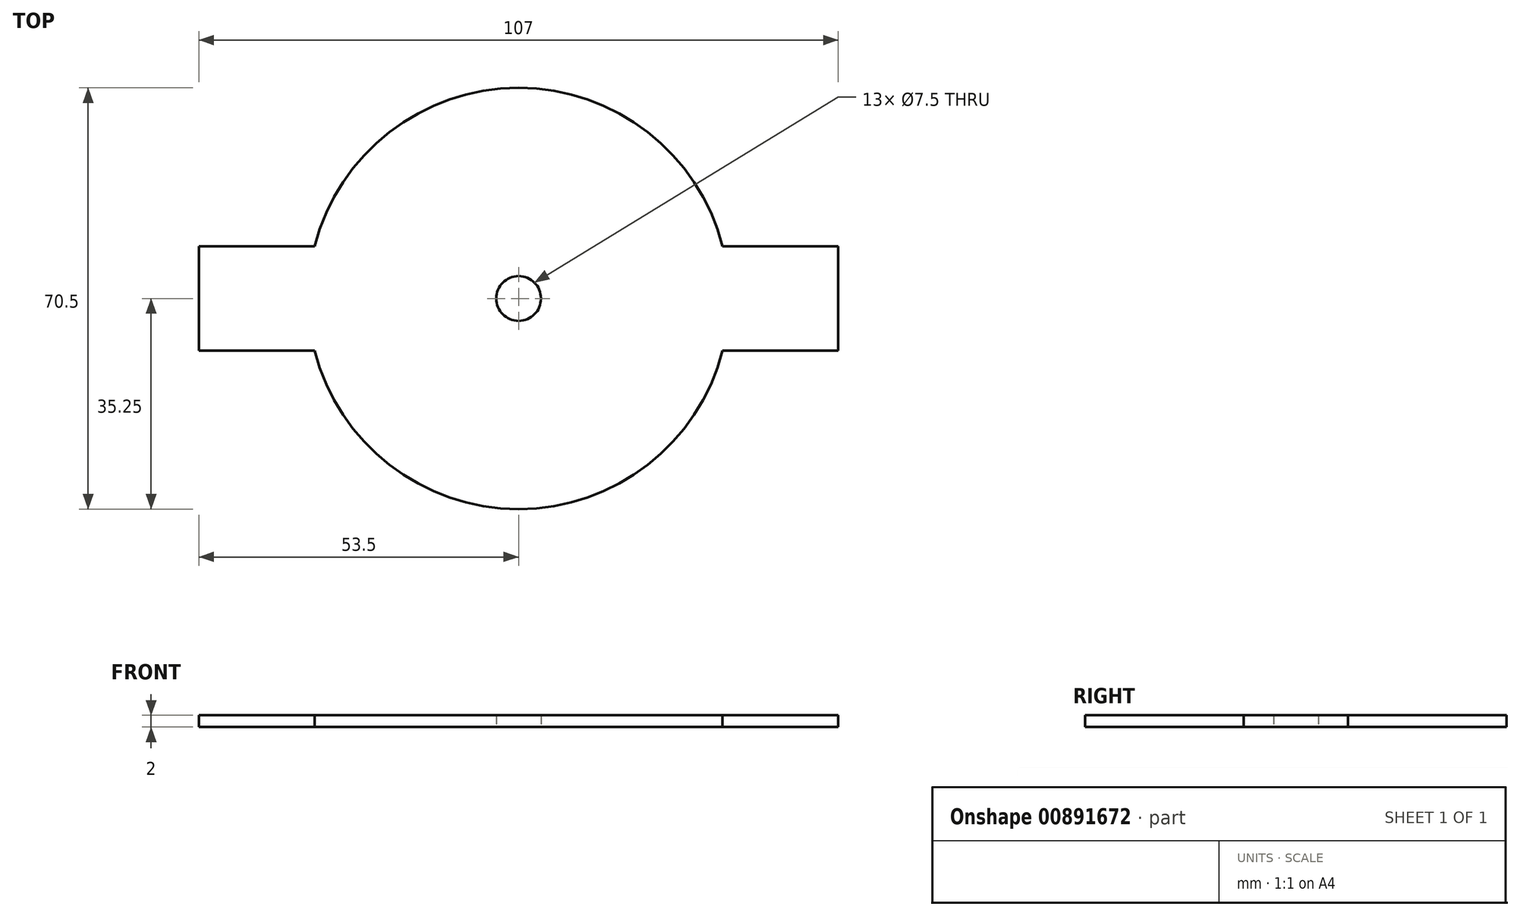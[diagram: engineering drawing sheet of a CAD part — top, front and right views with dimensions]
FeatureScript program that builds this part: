
annotation { "Feature Type Name" : "Feature", "Feature Type Description" : "" }
export const myFeature = defineFeature(function(context is Context, id is Id, definition is map)
    precondition{}
    {
        {
            var Q0;
            Q0=qCreatedBy(makeId("Top.planeOp"),FACE);
            var sketch = newSketch(context, id + "F0", { "sketchPlane" : qUnion([Q0])});
            skArc(sketch, "E0", {"start": v(-34.15, -8.75) * mm, "mid": v(0, -35.25) * mm, "end": v(34.15, -8.75) * mm});
            skLineSegment(sketch, "E1.bottom", {"start": v(-53.5, -8.75) * mm, "end": v(-34.15, -8.75) * mm});
            skLineSegment(sketch, "E1.top", {"start": v(-53.5, 8.75) * mm, "end": v(-34.15, 8.75) * mm});
            skLineSegment(sketch, "E1.left", {"start": v(-53.5, -8.75) * mm, "end": v(-53.5, 8.75) * mm});
            skLineSegment(sketch, "E1.right", {"start": v(53.5, -8.75) * mm, "end": v(53.5, 8.75) * mm});
            skLineSegment(sketch, "E2.trimOffspring", {"start": v(34.15, 8.75) * mm, "end": v(53.5, 8.75) * mm});
            skLineSegment(sketch, "E3.trimOffspring", {"start": v(34.15, -8.75) * mm, "end": v(53.5, -8.75) * mm});
            skArc(sketch, "E4.trimOffspring", {"start": v(34.15, 8.75) * mm, "mid": v(0, 35.25) * mm, "end": v(-34.15, 8.75) * mm});
            skCircle(sketch, "E5", {"center": v(0, 0) * mm, "radius": 3.75 * mm});
            skSolve(sketch);
        }
        {
            var Q0;
            Q0=makeQuery(id+"F0.imprint","IMPRINT",FACE,{"disambiguationData":[TD([[makeQuery(id+"F0.imprint","IMPRINT",EDGE,{"derivedFrom":sQuery(id+"F0.wireOp",EDGE,"E0")}),1.0]])]});
            extrude(context, id + "F1", {"entities" : qUnion([Q0]), "depth" : 2 * mm, "offsetDistance" : 25 * mm});
        }
    });
